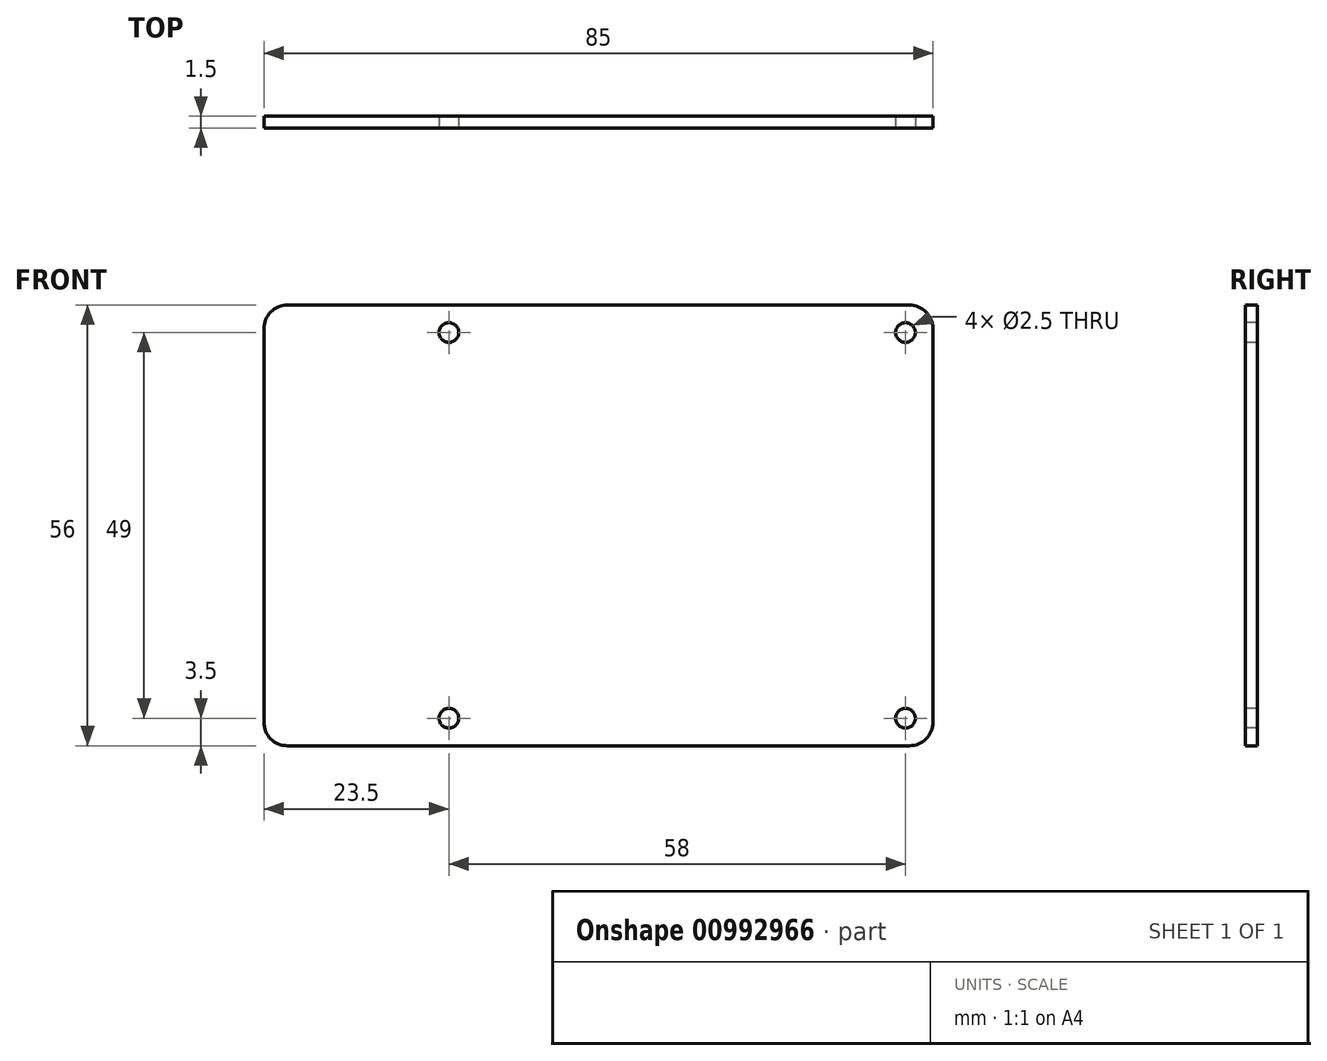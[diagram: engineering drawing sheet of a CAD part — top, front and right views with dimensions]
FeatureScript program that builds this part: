
annotation { "Feature Type Name" : "Feature", "Feature Type Description" : "" }
export const myFeature = defineFeature(function(context is Context, id is Id, definition is map)
    precondition{}
    {
        {
            var Q0;
            Q0=qCreatedBy(makeId("Front.planeOp"),FACE);
            var sketch = newSketch(context, id + "F0", { "sketchPlane" : qUnion([Q0])});
            skLineSegment(sketch, "E0.bottom", {"start": v(42.5, 28) * mm, "end": v(-42.5, 28) * mm});
            skLineSegment(sketch, "E0.top", {"start": v(42.5, -28) * mm, "end": v(-42.5, -28) * mm});
            skLineSegment(sketch, "E0.left", {"start": v(42.5, 28) * mm, "end": v(42.5, -28) * mm});
            skLineSegment(sketch, "E0.right", {"start": v(-42.5, 28) * mm, "end": v(-42.5, -28) * mm});
            skPoint(sketch, "E0.middle", {"position": v(0, 0) * mm});
            skSolve(sketch);
        }
        {
            var Q0;
            Q0 = qSketchRegion(id + "F0", true);
            extrude(context, id + "F1", {"entities" : qUnion([Q0]), "depth" : 1.5 * mm, "offsetDistance" : 25.4 * mm});
        }
        {
            var Q0;
            Q0=makeQuery(id+"F1.opExtrude","SWEPT_EDGE",EDGE,{"disambiguationData":[OSD([sQuery(id+"F0.wireOp",EDGE,"E0.bottom"),sQuery(id+"F0.wireOp",EDGE,"E0.right")])]});
            var Q1;
            Q1=makeQuery(id+"F1.opExtrude","SWEPT_EDGE",EDGE,{"disambiguationData":[OSD([sQuery(id+"F0.wireOp",EDGE,"E0.bottom"),sQuery(id+"F0.wireOp",EDGE,"E0.left")])]});
            var Q2;
            Q2=makeQuery(id+"F1.opExtrude","SWEPT_EDGE",EDGE,{"disambiguationData":[OSD([sQuery(id+"F0.wireOp",EDGE,"E0.top"),sQuery(id+"F0.wireOp",EDGE,"E0.left")])]});
            var Q3;
            Q3=makeQuery(id+"F1.opExtrude","SWEPT_EDGE",EDGE,{"disambiguationData":[OSD([sQuery(id+"F0.wireOp",EDGE,"E0.top"),sQuery(id+"F0.wireOp",EDGE,"E0.right")])]});
            fillet(context, id + "F2", {"entities" : qUnion([Q0, Q1, Q2, Q3]), "radius" : 3 * mm, "tangentPropagation" : true, "allowEdgeOverflow" : false});
        }
        {
            var Q0;
            Q0=makeQuery(id+"F1.opExtrude","CAP_FACE",FACE,{"disambiguationData":[OSD([sQuery(id+"F0.wireOp",EDGE,"E0.bottom"),sQuery(id+"F0.wireOp",EDGE,"E0.top"),sQuery(id+"F0.wireOp",EDGE,"E0.left"),sQuery(id+"F0.wireOp",EDGE,"E0.right")])],"isStart":false});
            var sketch = newSketch(context, id + "F3", { "sketchPlane" : qUnion([Q0])});
            skCircle(sketch, "E1", {"center": v(39, 24.5) * mm, "radius": 1.25 * mm});
            skCircle(sketch, "E2", {"center": v(-19, 24.5) * mm, "radius": 1.25 * mm});
            skCircle(sketch, "E3.MirrorC", {"center": v(-19, -24.5) * mm, "radius": 1.25 * mm});
            skCircle(sketch, "E4.MirrorC", {"center": v(39, -24.5) * mm, "radius": 1.25 * mm});
            skSolve(sketch);
        }
        {
            var Q0;
            Q0 = qSketchRegion(id + "F3", true);
            extrude(context, id + "F4", {"entities" : qUnion([Q0]), "operationType" : NewBodyOperationType.REMOVE, "endBound" : BoundingType.THROUGH_ALL, "oppositeDirection" : true, "depth" : 25.4 * mm, "offsetDistance" : 25.4 * mm});
        }
    });
